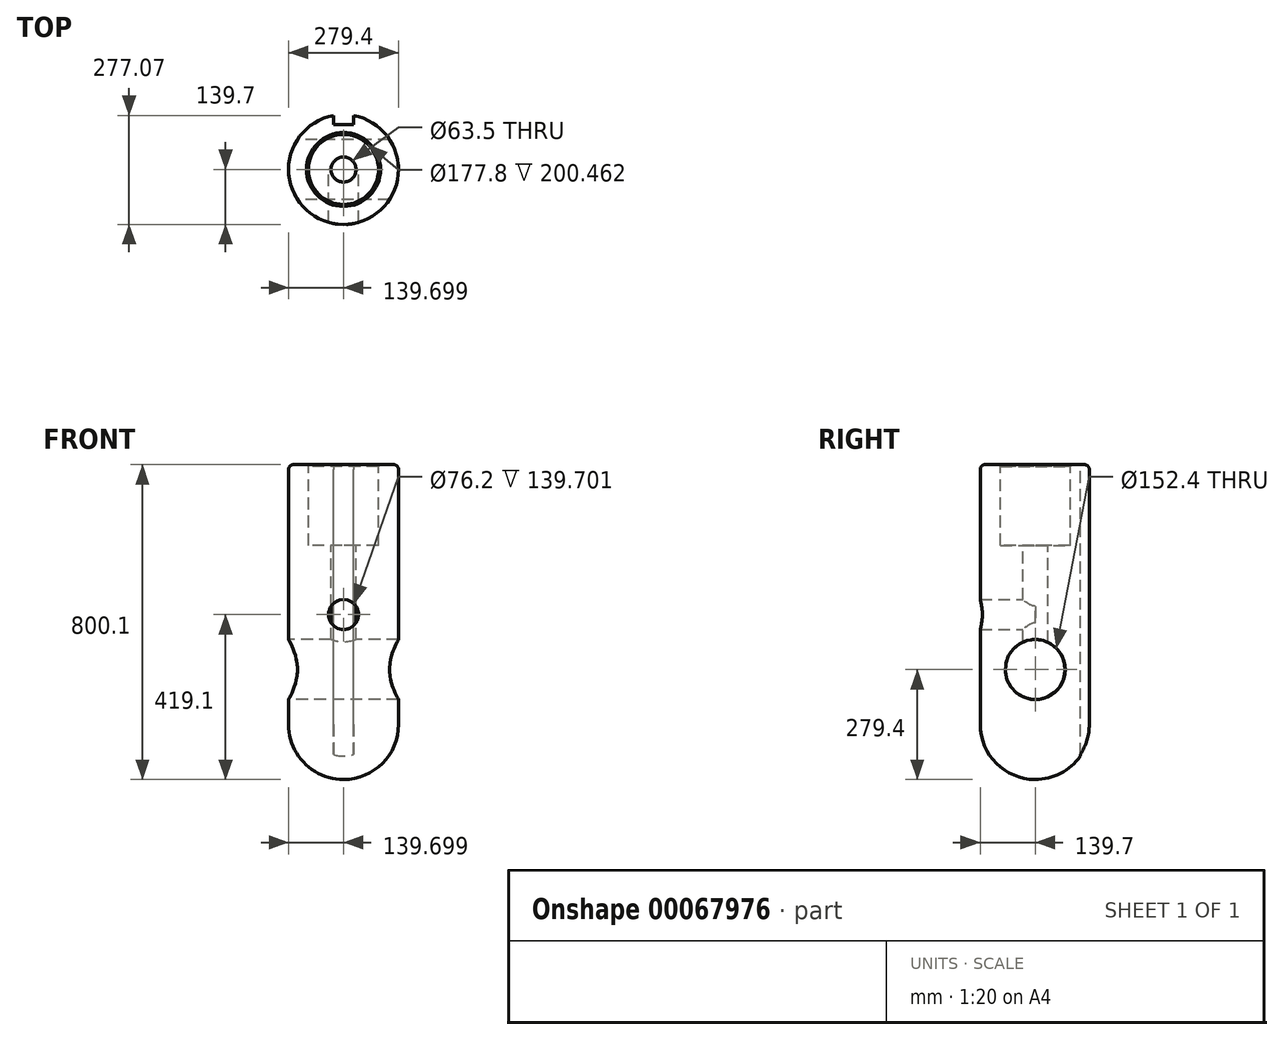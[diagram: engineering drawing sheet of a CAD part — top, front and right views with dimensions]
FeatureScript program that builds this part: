
annotation { "Feature Type Name" : "Feature", "Feature Type Description" : "" }
export const myFeature = defineFeature(function(context is Context, id is Id, definition is map)
    precondition{}
    {
        {
            var Q0;
            Q0=qCreatedBy(makeId("Front.planeOp"),FACE);
            var sketch = newSketch(context, id + "F0", { "sketchPlane" : qUnion([Q0])});
            skLineSegment(sketch, "E0", {"start": v(113.84, 454.86) * mm, "end": v(202.74, 454.86) * mm});
            skLineSegment(sketch, "E1", {"start": v(202.74, 454.86) * mm, "end": v(202.74, 660.4) * mm});
            skLineSegment(sketch, "E2", {"start": v(202.74, 660.4) * mm, "end": v(240.84, 660.4) * mm});
            skLineSegment(sketch, "E3", {"start": v(253.54, 647.7) * mm, "end": v(253.54, 0) * mm});
            skLineSegment(sketch, "E4", {"start": v(113.84, 454.86) * mm, "end": v(113.84, -139.7) * mm});
            skArc(sketch, "E5", {"start": v(113.84, -139.7) * mm, "mid": v(212.62, -98.78) * mm, "end": v(253.54, 0) * mm});
            skPoint(sketch, "E6.visualSharp", {"position": v(253.54, 660.4) * mm});
            skArc(sketch, "E6.filletArc", {"start": v(253.54, 647.7) * mm, "mid": v(249.82, 656.68) * mm, "end": v(240.84, 660.4) * mm});
            skSolve(sketch);
        }
        {
            var Q0;
            Q0=makeQuery(id+"F0.imprint","IMPRINT",FACE,{"disambiguationData":[TD([[makeQuery(id+"F0.imprint","IMPRINT",EDGE,{"derivedFrom":sQuery(id+"F0.wireOp",EDGE,"E0")}),-1.0]])]});
            var Q1;
            Q1=sQuery(id+"F0.wireOp",EDGE,"E4");
            revolve(context, id + "F1", {"entities" : qUnion([Q0]), "axis" : qUnion([Q1]), "revolveType" : RevolveType.FULL});
        }
        {
            var Q0;
            Q0=makeQuery(id+"F1.opRevolve","SWEPT_EDGE",EDGE,{"disambiguationData":[OSD([sQuery(id+"F0.wireOp",EDGE,"E1"),sQuery(id+"F0.wireOp",EDGE,"E2")])]});
            chamfer(context, id + "F2", {"entities" : qUnion([Q0]), "width" : 5.08 * mm, "tangentPropagation" : true});
        }
        {
            var Q0;
            Q0=makeQuery(id+"F1.opRevolve","SWEPT_FACE",FACE,{"disambiguationData":[OSD([sQuery(id+"F0.wireOp",EDGE,"E2")])]});
            var sketch = newSketch(context, id + "F3", { "sketchPlane" : qUnion([Q0])});
            skLineSegment(sketch, "E7.bottom", {"start": v(88.44, 154.63) * mm, "end": v(139.24, 154.63) * mm});
            skLineSegment(sketch, "E7.top", {"start": v(88.44, 114.3) * mm, "end": v(139.24, 114.3) * mm});
            skLineSegment(sketch, "E7.left", {"start": v(88.44, 154.63) * mm, "end": v(88.44, 114.3) * mm});
            skLineSegment(sketch, "E7.right", {"start": v(139.24, 154.63) * mm, "end": v(139.24, 114.3) * mm});
            skSolve(sketch);
        }
        {
            var Q0;
            {var subQ0=sQuery(id+"F3.wireOp",EDGE,"E7.bottom");Q0=makeQuery(id+"F3.imprint","IMPRINT",FACE,{"disambiguationData":[TD([[makeQuery(id+"F3.imprint","IMPRINT",EDGE,{"derivedFrom":subQ0}),-1.0]])]});}
            var Q1;
            {var subQ0=sQuery(id+"F3.wireOp",EDGE,"E7.top");Q1=makeQuery(id+"F3.imprint","IMPRINT",FACE,{"disambiguationData":[TD([[makeQuery(id+"F3.imprint","IMPRINT",EDGE,{"derivedFrom":subQ0}),1.0]])]});}
            extrude(context, id + "F4", {"entities" : qUnion([Q0, Q1]), "operationType" : NewBodyOperationType.REMOVE, "oppositeDirection" : true, "depth" : 806.28 * mm});
        }
        {
            var Q0;
            Q0=qCreatedBy(makeId("Right.planeOp"),FACE);
            cPlane(context, id + "F5", {"entities" : qUnion([Q0]), "cplaneType" : CPlaneType.OFFSET, "offset" : 152.4 * mm, "oppositeDirection" : true, "width" : 152.4 * mm, "height" : 152.4 * mm});
        }
        {
            var Q0;
            Q0=qCreatedBy(id+"F5.planeOp",FACE);
            var sketch = newSketch(context, id + "F6", { "sketchPlane" : qUnion([Q0])});
            skCircle(sketch, "E8", {"center": v(0, 139.7) * mm, "radius": 76.2 * mm});
            skSolve(sketch);
        }
        {
            var Q0;
            Q0=makeQuery(id+"F6.imprint","IMPRINT",FACE,{"disambiguationData":[TD([[makeQuery(id+"F6.imprint","IMPRINT",EDGE,{"derivedFrom":sQuery(id+"F6.wireOp",EDGE,"E8")}),1.0]])]});
            extrude(context, id + "F7", {"entities" : qUnion([Q0]), "operationType" : NewBodyOperationType.REMOVE, "depth" : 635.34 * mm});
        }
        {
            var Q0;
            Q0=makeQuery(id+"F1.opRevolve","SWEPT_FACE",FACE,{"disambiguationData":[OSD([sQuery(id+"F0.wireOp",EDGE,"E0")])]});
            var sketch = newSketch(context, id + "F8", { "sketchPlane" : qUnion([Q0])});
            skCircle(sketch, "E9", {"center": v(113.84, 0) * mm, "radius": 31.75 * mm});
            skSolve(sketch);
        }
        {
            var Q0;
            Q0=makeQuery(id+"F8.imprint","IMPRINT",FACE,{"disambiguationData":[TD([[makeQuery(id+"F8.imprint","IMPRINT",EDGE,{"derivedFrom":sQuery(id+"F8.wireOp",EDGE,"E9")}),1.0]])]});
            extrude(context, id + "F9", {"entities" : qUnion([Q0]), "operationType" : NewBodyOperationType.REMOVE, "oppositeDirection" : true, "depth" : 343.57 * mm});
        }
        {
            var Q0;
            Q0=qCreatedBy(makeId("Front.planeOp"),FACE);
            var sketch = newSketch(context, id + "F10", { "sketchPlane" : qUnion([Q0])});
            skCircle(sketch, "E10", {"center": v(113.84, 279.4) * mm, "radius": 38.1 * mm});
            skSolve(sketch);
        }
        {
            var Q0;
            Q0 = qSketchRegion(id + "F10", true);
            extrude(context, id + "F11", {"entities" : qUnion([Q0]), "operationType" : NewBodyOperationType.REMOVE, "depth" : 418.6 * mm});
        }
    });
